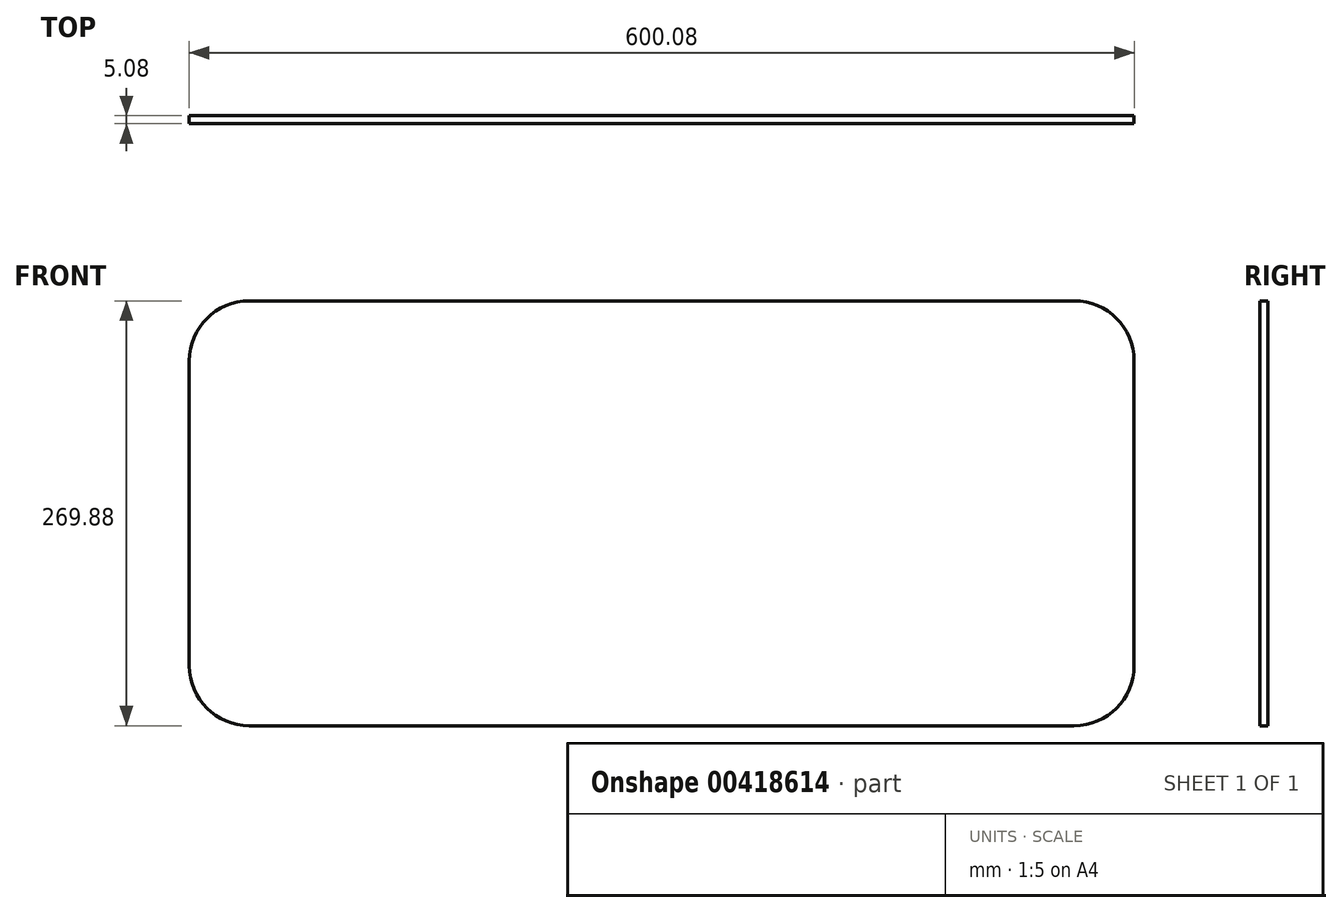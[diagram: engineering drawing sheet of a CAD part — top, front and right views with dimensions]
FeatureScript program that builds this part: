
annotation { "Feature Type Name" : "Feature", "Feature Type Description" : "" }
export const myFeature = defineFeature(function(context is Context, id is Id, definition is map)
    precondition{}
    {
        {
            var Q0;
            Q0=qCreatedBy(makeId("Front.planeOp"),FACE);
            var sketch = newSketch(context, id + "F0", { "sketchPlane" : qUnion([Q0])});
            skLineSegment(sketch, "E0.bottom", {"start": v(0, 0) * mm, "end": v(600.08, 0) * mm});
            skLineSegment(sketch, "E1", {"start": v(0, 0) * mm, "end": v(0, 269.88) * mm});
            skLineSegment(sketch, "E2", {"start": v(0, 269.88) * mm, "end": v(600.08, 269.88) * mm});
            skLineSegment(sketch, "E3", {"start": v(600.08, 269.88) * mm, "end": v(600.08, 0) * mm});
            skSolve(sketch);
        }
        {
            var Q0;
            Q0=makeQuery(id+"F0.imprint","IMPRINT",FACE,{"disambiguationData":[TD([[makeQuery(id+"F0.imprint","IMPRINT",EDGE,{"derivedFrom":sQuery(id+"F0.wireOp",EDGE,"E0.bottom")}),1.0]])]});
            extrude(context, id + "F1", {"entities" : qUnion([Q0]), "depth" : 5.08 * mm});
        }
        {
            var Q0;
            Q0=makeQuery(id+"F1.opExtrude","SWEPT_EDGE",EDGE,{"disambiguationData":[OSD([sQuery(id+"F0.wireOp",EDGE,"E0.bottom"),sQuery(id+"F0.wireOp",EDGE,"E3")])]});
            fillet(context, id + "F2", {"entities" : qUnion([Q0]), "radius" : 38.1 * mm, "tangentPropagation" : true, "allowEdgeOverflow" : false});
        }
        {
            var Q0;
            Q0=makeQuery(id+"F1.opExtrude","SWEPT_EDGE",EDGE,{"disambiguationData":[OSD([sQuery(id+"F0.wireOp",EDGE,"E0.bottom"),sQuery(id+"F0.wireOp",EDGE,"E1")])]});
            fillet(context, id + "F3", {"entities" : qUnion([Q0]), "radius" : 38.1 * mm, "tangentPropagation" : true, "allowEdgeOverflow" : false});
        }
        {
            var Q0;
            Q0=makeQuery(id+"F1.opExtrude","SWEPT_EDGE",EDGE,{"disambiguationData":[OSD([sQuery(id+"F0.wireOp",EDGE,"E1"),sQuery(id+"F0.wireOp",EDGE,"E2")])]});
            fillet(context, id + "F4", {"entities" : qUnion([Q0]), "radius" : 38.1 * mm, "tangentPropagation" : true, "allowEdgeOverflow" : false});
        }
        {
            var Q0;
            Q0=makeQuery(id+"F1.opExtrude","SWEPT_EDGE",EDGE,{"disambiguationData":[OSD([sQuery(id+"F0.wireOp",EDGE,"E2"),sQuery(id+"F0.wireOp",EDGE,"E3")])]});
            fillet(context, id + "F5", {"entities" : qUnion([Q0]), "radius" : 38.1 * mm, "tangentPropagation" : true, "allowEdgeOverflow" : false});
        }
    });
